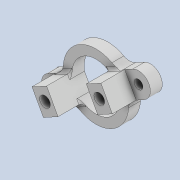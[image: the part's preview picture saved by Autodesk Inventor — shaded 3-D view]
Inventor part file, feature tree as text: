
AUTODESK INVENTOR PART (.ipt)
format: ipt  version: 2020 (Build 240168000, 168)  size: 216,064 bytes
history: native  units: mm
features: other x5, extrude x4, sketch x3, fillet x2, reference x2, projected_geometry x2, plane x1
ambient origin geometry x8: Origin, YZ Plane, XZ Plane, XY Plane, X Axis, Y Axis, Z Axis, Center Point
bodies: Solid1 (feature_tree)
feature tree (19):
  extrude  "Extrusion1"  Depth=8.0mm
  extrude  "Extrusion3"  Depth=2.0mm TaperAngle=0.0deg
  sketch  "Sketch5"  dims[d7=5.2mm d8=5.2mm d9=1.8mm d10=1.8mm d11=2.0mm d12=0.0mm d13=4.0mm d14=2.8mm d15=4.0mm d16=2.8mm d17=2.0mm d18=0.0mm d19=4.0mm d20=0.0mm d21=2.0mm d25=0.5mm]
  extrude  "Extrusion4"  Depth=0.5mm
  plane  "Work Plane1"
  extrude  "Extrusion5"  Depth=0.5mm
  fillet  "Fillet1"  Radius=1.8mm
  fillet  "Fillet2"  Radius=2.0mm
  sketch  "Sketch1"  dims[d0=4.0mm d1=8.0mm]
  reference  "Reference1"
  reference  "Reference2"
  sketch  "Sketch4"  dims[d2=11.0mm d3=2.0mm d4=0.0mm]
  projected_geometry  "Projected Loop2"
  projected_geometry  "Projected Loop3"
  parser-record x1  (decoder bookkeeping rows leaked as tree rows — omitted from the tree; the rows remain in map.json)
  other  "tip_ass_t1.iam"
  other  "pin_conn_1:1"
  other  "motor_1608:1"
  other  "motor_1608_inner:1"
note: 1 file-system path scrubbed to <path> (originals preserved in map.json)
